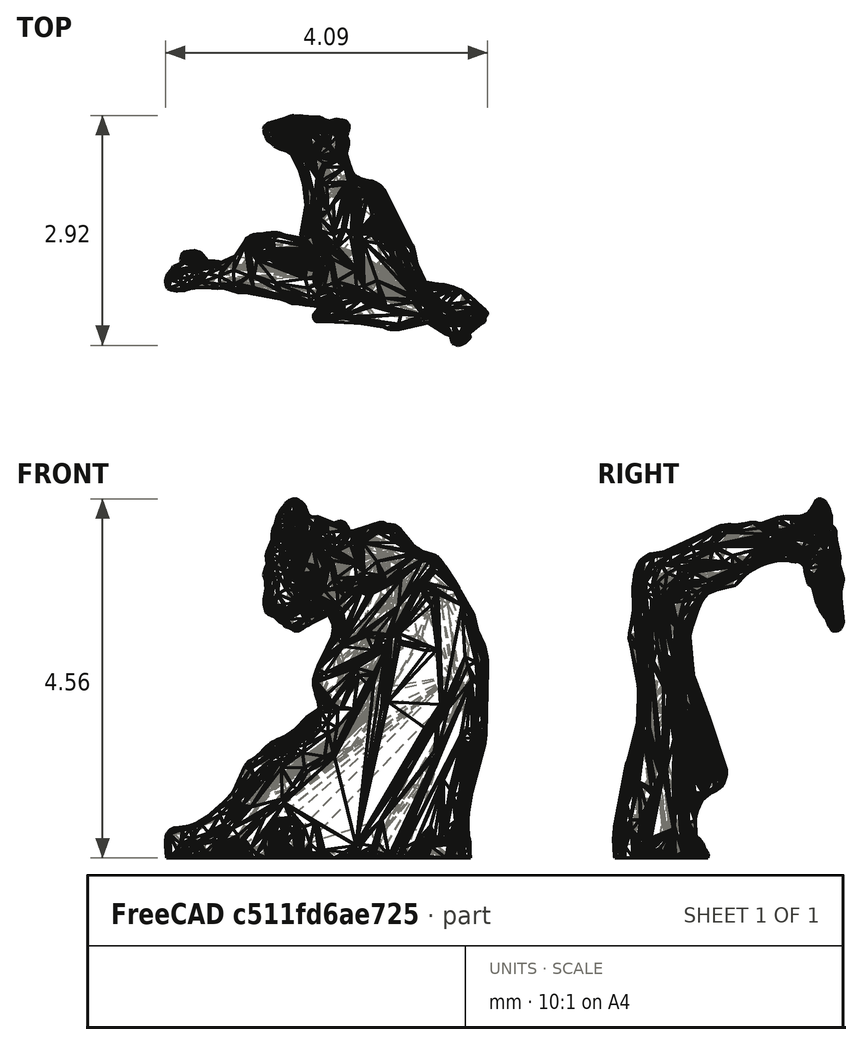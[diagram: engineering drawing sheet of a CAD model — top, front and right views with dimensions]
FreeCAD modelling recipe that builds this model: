
FCSTD DOCUMENT  (FreeCAD 0.20R29603 (Git))
Label: pwp
License: All rights reserved
LicenseURL: http://en.wikipedia.org/wiki/All_rights_reserved
objects: Mesh::Feature×2, Part::Feature×1, PartDesign::FeatureBase×1, PartDesign::Plane×1, Sketcher::SketchObject×1, PartDesign::Line×1, PartDesign::Point×1, PartDesign::Body×1
note: 7 computed .brp shape members not serialized (recipe doc carries the construction recipe); baked Part::Feature solids carry a one-line shape summary decoded from their .brp

FEATURE [Mesh::Feature] pwp
FEATURE [Part::Feature] pwp001
  shape: bbox 4.093 x 2.918 x 4.562 mm, 7946 faces, 0 solids (baked)
FEATURE [Mesh::Feature] ii_sclerite
FEATURE [PartDesign::FeatureBase] BaseFeature
  BaseFeature = -> pwp001
FEATURE [PartDesign::Plane] DatumPlane  label="ii_sclerite_axis_DatumPlane"
  AttachmentOffset = pos=(0,0,-2.4) rot=(0,0,1;0rad)
  Length = 60
  MapMode = 5
  Placement = pos=(0,2.4,-5e-16) rot=(1,0,0;1.5708rad)
  ResizeMode = 0
  Support = -> [XZ_Plane]
  Width = 60
FEATURE [Sketcher::SketchObject] Sketch  label="ii_sclerite_axis_Sketch"
  FullyConstrained = true
  MapMode = 5
  Placement = pos=(0,2.4,-5e-16) rot=(0,0.707107,0.707107;3.14159rad)
  Support = -> [DatumPlane]
  sketch-geometry (4):
    g0: LineSegment StartX=0 StartY=0 StartZ=0 EndX=0 EndY=0.4599 EndZ=0
    g1: LineSegment StartX=0 StartY=0.4599 StartZ=0 EndX=0 EndY=3.0532 EndZ=0
    g2: LineSegment StartX=-4.24024 StartY=5.7028 StartZ=0 EndX=4.24024 EndY=0.403604 EndZ=0
    g3: GeomPoint X=0 Y=3.0532 Z=0
  constraints (10):
    c: Vertical(g0)
    c: Coincident(g0,g-1)
    c: DistanceY(g0,g0) = 0.4599
    c: Coincident(g1,g0)
    c: Vertical(g1)
    c: DistanceY(g1,g1) = 2.5933
    c: Distance(g2,g2) = 10
    c: Symmetric(g2,g2,g1)
    c: Angle(g2,g-1) = 0.558505
    c: Coincident(g3,g1)
FEATURE [PartDesign::Line] DatumLine  label="ii_sclerite_axis_DatumLine"
  AttacherType = Attacher::AttachEngineLine
  Length = 20
  MapMode = 29
  Placement = pos=(-1.3721,2.4,2.19582) rot=(0.658342,-0.658342,-0.364925;2.44177rad)
  ResizeMode = 0
  Support = -> [Sketch]
FEATURE [PartDesign::Point] DatumPoint  label="ii_sclerite_axis_DatumPoint"
  AttacherType = Attacher::AttachEnginePoint
  MapMode = 37
  Placement = pos=(0,2.4,3.0532) rot=(0,0,1;0rad)
  Support = -> [Sketch]
FEATURE [PartDesign::Body] Body  label="pwp_Body"
  BaseFeature = -> pwp001
  Group = -> [BaseFeature,DatumPlane,Sketch,DatumLine,DatumPoint]
  Origin = -> Origin
  Tip = -> BaseFeature
